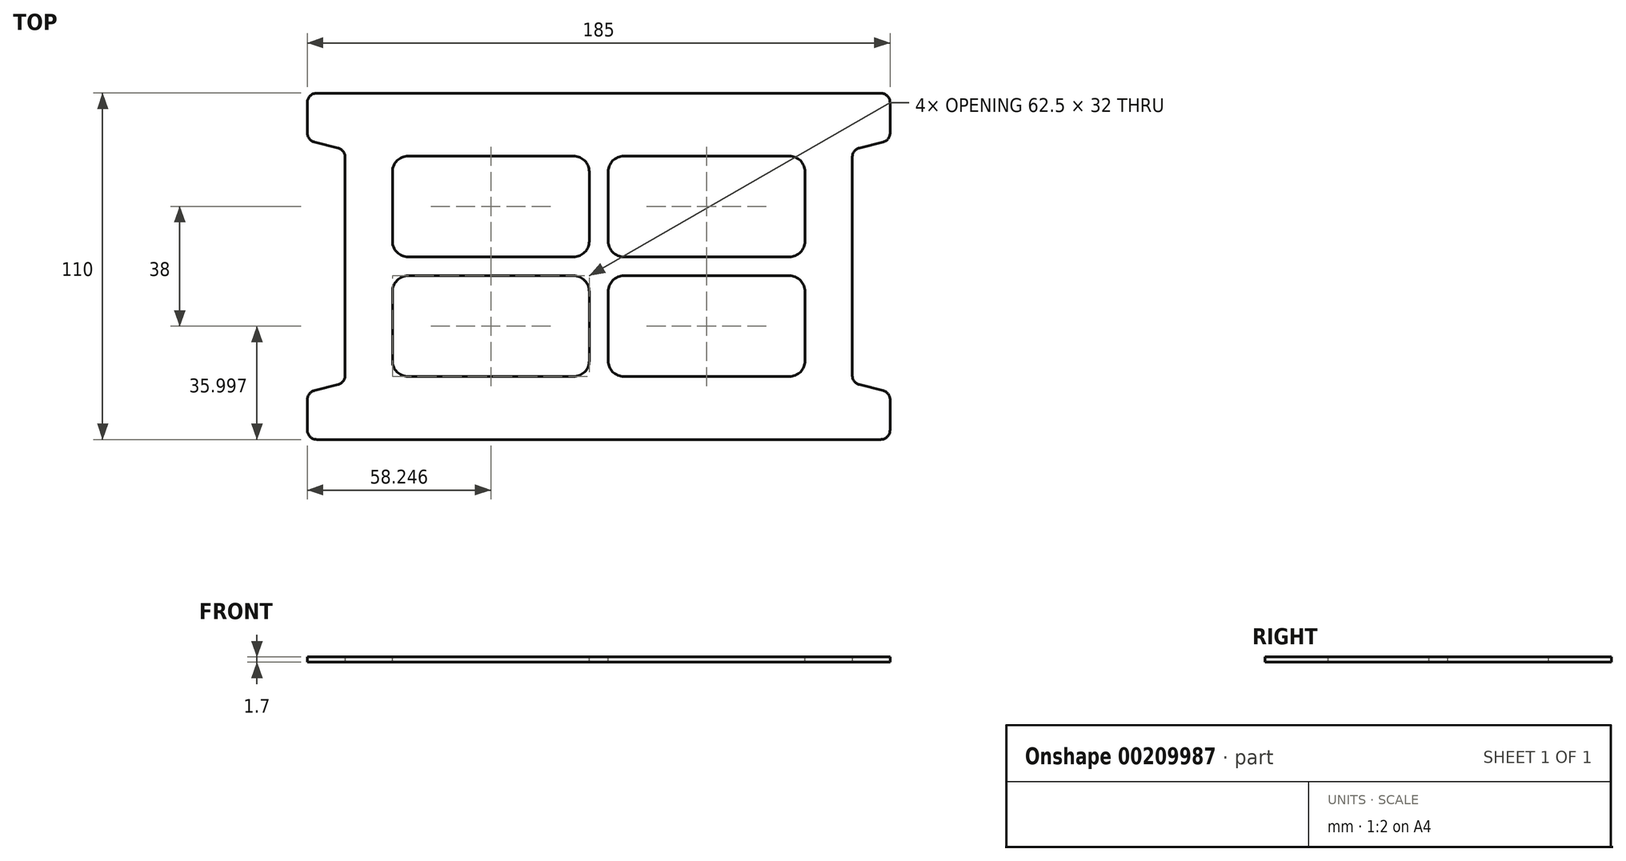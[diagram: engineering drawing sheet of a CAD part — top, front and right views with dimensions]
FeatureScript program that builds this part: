
annotation { "Feature Type Name" : "Feature", "Feature Type Description" : "" }
export const myFeature = defineFeature(function(context is Context, id is Id, definition is map)
    precondition{}
    {
        {
            var Q0;
            Q0=qCreatedBy(makeId("Top.planeOp"),FACE);
            var sketch = newSketch(context, id + "F0", { "sketchPlane" : qUnion([Q0])});
            skLineSegment(sketch, "E0", {"start": v(-84.92, 54.25) * mm, "end": v(100.08, 54.25) * mm});
            skLineSegment(sketch, "E1", {"start": v(100.08, 54.25) * mm, "end": v(100.08, 39.25) * mm});
            skLineSegment(sketch, "E2", {"start": v(100.08, 39.25) * mm, "end": v(88.08, 39.25) * mm});
            skLineSegment(sketch, "E3", {"start": v(88.08, 39.25) * mm, "end": v(88.08, -40.75) * mm});
            skLineSegment(sketch, "E4", {"start": v(100.08, -40.75) * mm, "end": v(100.08, -55.75) * mm});
            skLineSegment(sketch, "E5", {"start": v(100.08, -55.75) * mm, "end": v(-84.92, -55.75) * mm});
            skLineSegment(sketch, "E6", {"start": v(-84.92, -40.75) * mm, "end": v(-72.92, -40.75) * mm});
            skLineSegment(sketch, "E7", {"start": v(-72.92, -40.75) * mm, "end": v(-72.92, 39.25) * mm});
            skLineSegment(sketch, "E8", {"start": v(-72.92, 39.25) * mm, "end": v(-84.92, 39.25) * mm});
            skLineSegment(sketch, "E9", {"start": v(-84.92, 39.25) * mm, "end": v(-84.92, 54.25) * mm});
            skLineSegment(sketch, "E10", {"start": v(-84.92, -40.75) * mm, "end": v(-84.92, -55.75) * mm});
            skLineSegment(sketch, "E11", {"start": v(100.08, 39.25) * mm, "end": v(88.08, 36.25) * mm});
            skLineSegment(sketch, "E12", {"start": v(-84.92, 39.25) * mm, "end": v(-72.92, 36.25) * mm});
            skLineSegment(sketch, "E13", {"start": v(7.58, 54.25) * mm, "end": v(7.58, -55.75) * mm, "construction": true});
            skLineSegment(sketch, "E14", {"start": v(88.08, -0.75) * mm, "end": v(-72.92, -0.75) * mm, "construction": true});
            skLineSegment(sketch, "E15.MirrorCS", {"start": v(100.08, -40.75) * mm, "end": v(88.08, -37.75) * mm});
            skLineSegment(sketch, "E16.MirrorCS", {"start": v(-84.92, -40.75) * mm, "end": v(-72.92, -37.75) * mm});
            skSolve(sketch);
        }
        {
            var Q0;
            Q0=makeQuery(id+"F0.imprint","IMPRINT",FACE,{"disambiguationData":[TD([[makeQuery(id+"F0.imprint","IMPRINT",EDGE,{"derivedFrom":sQuery(id+"F0.wireOp",EDGE,"E0")}),-1.0]])]});
            var Q1;
            {var subQ0=sQuery(id+"F0.wireOp",EDGE,"E2");Q1=makeQuery(id+"F0.imprint","IMPRINT",FACE,{"disambiguationData":[TD([[makeQuery(id+"F0.imprint","IMPRINT",EDGE,{"derivedFrom":subQ0}),1.0]])]});}
            var Q2;
            {var subQ0=sQuery(id+"F0.wireOp",EDGE,"E8");Q2=makeQuery(id+"F0.imprint","IMPRINT",FACE,{"disambiguationData":[TD([[makeQuery(id+"F0.imprint","IMPRINT",EDGE,{"derivedFrom":subQ0}),1.0]])]});}
            var Q3;
            {var subQ0=sQuery(id+"F0.wireOp",EDGE,"E6");Q3=makeQuery(id+"F0.imprint","IMPRINT",FACE,{"disambiguationData":[TD([[makeQuery(id+"F0.imprint","IMPRINT",EDGE,{"derivedFrom":subQ0}),1.0]])]});}
            extrude(context, id + "F1", {"entities" : qUnion([Q0, Q1, Q2, Q3]), "depth" : 1.7 * mm});
        }
        {
            var Q0;
            Q0=makeQuery(id+"F1.opExtrude","SWEPT_EDGE",EDGE,{"disambiguationData":[OSD([sQuery(id+"F0.wireOp",EDGE,"E7"),sQuery(id+"F0.wireOp",EDGE,"E8")])]});
            var Q1;
            Q1=makeQuery(id+"F1.opExtrude","SWEPT_EDGE",EDGE,{"disambiguationData":[OSD([sQuery(id+"F0.wireOp",EDGE,"E8"),sQuery(id+"F0.wireOp",EDGE,"E9")])]});
            var Q2;
            Q2=makeQuery(id+"F1.opExtrude","SWEPT_EDGE",EDGE,{"disambiguationData":[OSD([sQuery(id+"F0.wireOp",EDGE,"E6"),sQuery(id+"F0.wireOp",EDGE,"E10")])]});
            var Q3;
            Q3=makeQuery(id+"F1.opExtrude","SWEPT_EDGE",EDGE,{"disambiguationData":[OSD([sQuery(id+"F0.wireOp",EDGE,"mhs02ShZ-4stZ-Phh9-EZn1-VpfWEpMby84q"),sQuery(id+"F0.wireOp",EDGE,"E4")])]});
            var Q4;
            Q4=makeQuery(id+"F1.opExtrude","SWEPT_EDGE",EDGE,{"disambiguationData":[OSD([sQuery(id+"F0.wireOp",EDGE,"E3"),sQuery(id+"F0.wireOp",EDGE,"mhs02ShZ-4stZ-Phh9-EZn1-VpfWEpMby84q")])]});
            var Q5;
            Q5=makeQuery(id+"F1.opExtrude","SWEPT_EDGE",EDGE,{"disambiguationData":[OSD([sQuery(id+"F0.wireOp",EDGE,"E1"),sQuery(id+"F0.wireOp",EDGE,"E2")])]});
            var Q6;
            Q6=makeQuery(id+"F1.opExtrude","SWEPT_EDGE",EDGE,{"disambiguationData":[OSD([sQuery(id+"F0.wireOp",EDGE,"E2"),sQuery(id+"F0.wireOp",EDGE,"E3")])]});
            var Q7;
            Q7=makeQuery(id+"F1.opExtrude","SWEPT_EDGE",EDGE,{"disambiguationData":[OSD([sQuery(id+"F0.wireOp",EDGE,"E6"),sQuery(id+"F0.wireOp",EDGE,"E7")])]});
            var Q8;
            Q8=makeQuery(id+"F1.opExtrude","SWEPT_EDGE",EDGE,{"disambiguationData":[OSD([sQuery(id+"F0.wireOp",EDGE,"E5"),sQuery(id+"F0.wireOp",EDGE,"E10")])]});
            var Q9;
            Q9=makeQuery(id+"F1.opExtrude","SWEPT_EDGE",EDGE,{"disambiguationData":[OSD([sQuery(id+"F0.wireOp",EDGE,"E0"),sQuery(id+"F0.wireOp",EDGE,"E9")])]});
            var Q10;
            Q10=makeQuery(id+"F1.opExtrude","SWEPT_EDGE",EDGE,{"disambiguationData":[OSD([sQuery(id+"F0.wireOp",EDGE,"E0"),sQuery(id+"F0.wireOp",EDGE,"E1")])]});
            fillet(context, id + "F2", {"entities" : qUnion([Q0, Q1, Q2, Q3, Q4, Q5, Q6, Q7, Q8, Q9, Q10]), "radius" : 3 * mm, "tangentPropagation" : true, "allowEdgeOverflow" : false});
        }
        {
            var Q0;
            Q0=makeQuery(id+"F1.opExtrude","CAP_FACE",FACE,{"disambiguationData":[OSD([sQuery(id+"F0.wireOp",EDGE,"E0"),sQuery(id+"F0.wireOp",EDGE,"E1"),sQuery(id+"F0.wireOp",EDGE,"E3"),sQuery(id+"F0.wireOp",EDGE,"E4"),sQuery(id+"F0.wireOp",EDGE,"E5"),sQuery(id+"F0.wireOp",EDGE,"E7"),sQuery(id+"F0.wireOp",EDGE,"E9"),sQuery(id+"F0.wireOp",EDGE,"E10"),sQuery(id+"F0.wireOp",EDGE,"E11"),sQuery(id+"F0.wireOp",EDGE,"E15.MirrorCS"),sQuery(id+"F0.wireOp",EDGE,"E12"),sQuery(id+"F0.wireOp",EDGE,"E16.MirrorCS")])],"isStart":false});
            var sketch = newSketch(context, id + "F3", { "sketchPlane" : qUnion([Q0])});
            skLineSegment(sketch, "E17.bottom", {"start": v(-57.92, 34.25) * mm, "end": v(4.58, 34.25) * mm});
            skLineSegment(sketch, "E17.top", {"start": v(-57.92, -35.75) * mm, "end": v(4.58, -35.75) * mm});
            skLineSegment(sketch, "E17.left", {"start": v(-57.92, 34.25) * mm, "end": v(-57.92, 2.25) * mm});
            skLineSegment(sketch, "E17.right", {"start": v(73.08, 34.25) * mm, "end": v(73.08, 2.25) * mm});
            skLineSegment(sketch, "E18", {"start": v(7.58, -35.75) * mm, "end": v(7.58, 34.25) * mm, "construction": true});
            skLineSegment(sketch, "E19", {"start": v(-57.92, -0.75) * mm, "end": v(73.08, -0.75) * mm, "construction": true});
            skLineSegment(sketch, "E20", {"start": v(4.58, -35.75) * mm, "end": v(4.58, -3.75) * mm});
            skLineSegment(sketch, "E21", {"start": v(10.58, -35.75) * mm, "end": v(10.58, -3.75) * mm});
            skLineSegment(sketch, "E22", {"start": v(-57.92, -3.75) * mm, "end": v(4.58, -3.75) * mm});
            skLineSegment(sketch, "E23", {"start": v(-57.92, 2.25) * mm, "end": v(4.58, 2.25) * mm});
            skLineSegment(sketch, "E24.trimOffspring", {"start": v(4.58, 2.25) * mm, "end": v(4.58, 34.25) * mm});
            skLineSegment(sketch, "E25.trimOffspring", {"start": v(10.58, -3.75) * mm, "end": v(73.08, -3.75) * mm});
            skLineSegment(sketch, "E26.trimOffspring", {"start": v(10.58, 2.25) * mm, "end": v(10.58, 34.25) * mm});
            skLineSegment(sketch, "E27.trimOffspring", {"start": v(10.58, 2.25) * mm, "end": v(73.08, 2.25) * mm});
            skLineSegment(sketch, "E28.trimOffspring", {"start": v(73.08, -3.75) * mm, "end": v(73.08, -35.75) * mm});
            skLineSegment(sketch, "E29.trimOffspring", {"start": v(10.58, -35.75) * mm, "end": v(73.08, -35.75) * mm});
            skLineSegment(sketch, "E30.trimOffspring", {"start": v(-57.92, -3.75) * mm, "end": v(-57.92, -35.75) * mm});
            skLineSegment(sketch, "E31.trimOffspring", {"start": v(10.58, 34.25) * mm, "end": v(73.08, 34.25) * mm});
            skSolve(sketch);
        }
        {
            var Q0;
            Q0 = qSketchRegion(id + "F3", true);
            extrude(context, id + "F4", {"entities" : qUnion([Q0]), "operationType" : NewBodyOperationType.REMOVE, "endBound" : BoundingType.THROUGH_ALL, "oppositeDirection" : true, "depth" : 25 * mm});
        }
        {
            var Q0;
            Q0=makeQuery(id+"F4.boolean.opBoolean","COPY",EDGE,{"derivedFrom":makeQuery(id+"F4.opExtrude","SWEPT_EDGE",EDGE,{"disambiguationData":[OSD([sQuery(id+"F3.wireOp",EDGE,"E17.bottom"),sQuery(id+"F3.wireOp",EDGE,"E17.left")])]})});
            var Q1;
            Q1=makeQuery(id+"F4.boolean.opBoolean","COPY",EDGE,{"derivedFrom":makeQuery(id+"F4.opExtrude","SWEPT_EDGE",EDGE,{"disambiguationData":[OSD([sQuery(id+"F3.wireOp",EDGE,"E17.bottom"),sQuery(id+"F3.wireOp",EDGE,"E17.right")])]})});
            var Q2;
            Q2=makeQuery(id+"F4.boolean.opBoolean","COPY",EDGE,{"derivedFrom":makeQuery(id+"F4.opExtrude","SWEPT_EDGE",EDGE,{"disambiguationData":[OSD([sQuery(id+"F3.wireOp",EDGE,"E17.top"),sQuery(id+"F3.wireOp",EDGE,"E17.right")])]})});
            var Q3;
            Q3=makeQuery(id+"F4.boolean.opBoolean","COPY",EDGE,{"derivedFrom":makeQuery(id+"F4.opExtrude","SWEPT_EDGE",EDGE,{"disambiguationData":[OSD([sQuery(id+"F3.wireOp",EDGE,"E17.top"),sQuery(id+"F3.wireOp",EDGE,"E17.left")])]})});
            var Q4;
            Q4=makeQuery(id+"F4.boolean.opBoolean","COPY",EDGE,{"derivedFrom":makeQuery(id+"F4.opExtrude","SWEPT_EDGE",EDGE,{"disambiguationData":[OSD([sQuery(id+"F3.wireOp",EDGE,"E23"),sQuery(id+"F3.wireOp",EDGE,"E24.trimOffspring")])]})});
            var Q5;
            Q5=makeQuery(id+"F4.boolean.opBoolean","COPY",EDGE,{"derivedFrom":makeQuery(id+"F4.opExtrude","SWEPT_EDGE",EDGE,{"disambiguationData":[OSD([sQuery(id+"F3.wireOp",EDGE,"E28.trimOffspring"),sQuery(id+"F3.wireOp",EDGE,"E29.trimOffspring")])]})});
            var Q6;
            Q6=makeQuery(id+"F4.boolean.opBoolean","COPY",EDGE,{"derivedFrom":makeQuery(id+"F4.opExtrude","SWEPT_EDGE",EDGE,{"disambiguationData":[OSD([sQuery(id+"F3.wireOp",EDGE,"E21"),sQuery(id+"F3.wireOp",EDGE,"E29.trimOffspring")])]})});
            var Q7;
            Q7=makeQuery(id+"F4.boolean.opBoolean","COPY",EDGE,{"derivedFrom":makeQuery(id+"F4.opExtrude","SWEPT_EDGE",EDGE,{"disambiguationData":[OSD([sQuery(id+"F3.wireOp",EDGE,"E26.trimOffspring"),sQuery(id+"F3.wireOp",EDGE,"E27.trimOffspring")])]})});
            var Q8;
            Q8=makeQuery(id+"F4.boolean.opBoolean","COPY",EDGE,{"derivedFrom":makeQuery(id+"F4.opExtrude","SWEPT_EDGE",EDGE,{"disambiguationData":[OSD([sQuery(id+"F3.wireOp",EDGE,"E21"),sQuery(id+"F3.wireOp",EDGE,"E25.trimOffspring")])]})});
            var Q9;
            Q9=makeQuery(id+"F4.boolean.opBoolean","COPY",EDGE,{"derivedFrom":makeQuery(id+"F4.opExtrude","SWEPT_EDGE",EDGE,{"disambiguationData":[OSD([sQuery(id+"F3.wireOp",EDGE,"E26.trimOffspring"),sQuery(id+"F3.wireOp",EDGE,"E31.trimOffspring")])]})});
            var Q10;
            Q10=makeQuery(id+"F4.boolean.opBoolean","COPY",EDGE,{"derivedFrom":makeQuery(id+"F4.opExtrude","SWEPT_EDGE",EDGE,{"disambiguationData":[OSD([sQuery(id+"F3.wireOp",EDGE,"E22"),sQuery(id+"F3.wireOp",EDGE,"E30.trimOffspring")])]})});
            var Q11;
            Q11=makeQuery(id+"F4.boolean.opBoolean","COPY",EDGE,{"derivedFrom":makeQuery(id+"F4.opExtrude","SWEPT_EDGE",EDGE,{"disambiguationData":[OSD([sQuery(id+"F3.wireOp",EDGE,"E20"),sQuery(id+"F3.wireOp",EDGE,"E22")])]})});
            var Q12;
            Q12=makeQuery(id+"F4.boolean.opBoolean","COPY",EDGE,{"derivedFrom":makeQuery(id+"F4.opExtrude","SWEPT_EDGE",EDGE,{"disambiguationData":[OSD([sQuery(id+"F3.wireOp",EDGE,"E25.trimOffspring"),sQuery(id+"F3.wireOp",EDGE,"E28.trimOffspring")])]})});
            fillet(context, id + "F5", {"entities" : qUnion([Q0, Q1, Q2, Q3, Q4, Q5, Q6, Q7, Q8, Q9, Q10, Q11, Q12]), "radius" : 5 * mm, "tangentPropagation" : true, "allowEdgeOverflow" : false});
        }
    });
